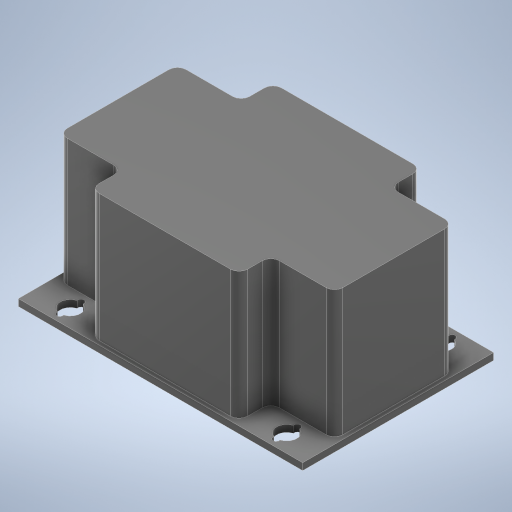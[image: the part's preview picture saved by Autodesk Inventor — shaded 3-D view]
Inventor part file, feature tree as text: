
AUTODESK INVENTOR PART (.ipt)
format: ipt  version: 2024.2 (Build 282272000, 272)  size: 311,808 bytes
history: native  units: mm
features: extrude x2, sketch x1, fillet x1
ambient origin geometry x8: Origin, YZ Plane, XZ Plane, XY Plane, X Axis, Y Axis, Z Axis, Center Point
bodies: Solid1 (feature_tree)
feature tree (4):
  sketch  "Sketch1"  dims[d0=45.0mm d1=67.0mm d7=1.6mm d8=0.0mm d9=31.6mm d10=0.0mm d18=2.0mm d19=4.8mm d33=51.0mm d34=36.5mm d38=1.0mm d43=1.0mm d44=1.0mm d46=6.5mm d47=1.5mm d48=1.0mm d50=16.0mm]
  extrude  "Extrusion1"  Depth=67.0mm
  extrude  "Extrusion2"  Depth=1.6mm TaperAngle=0.0deg
  fillet  "Fillet1"  Radius=31.6mm
